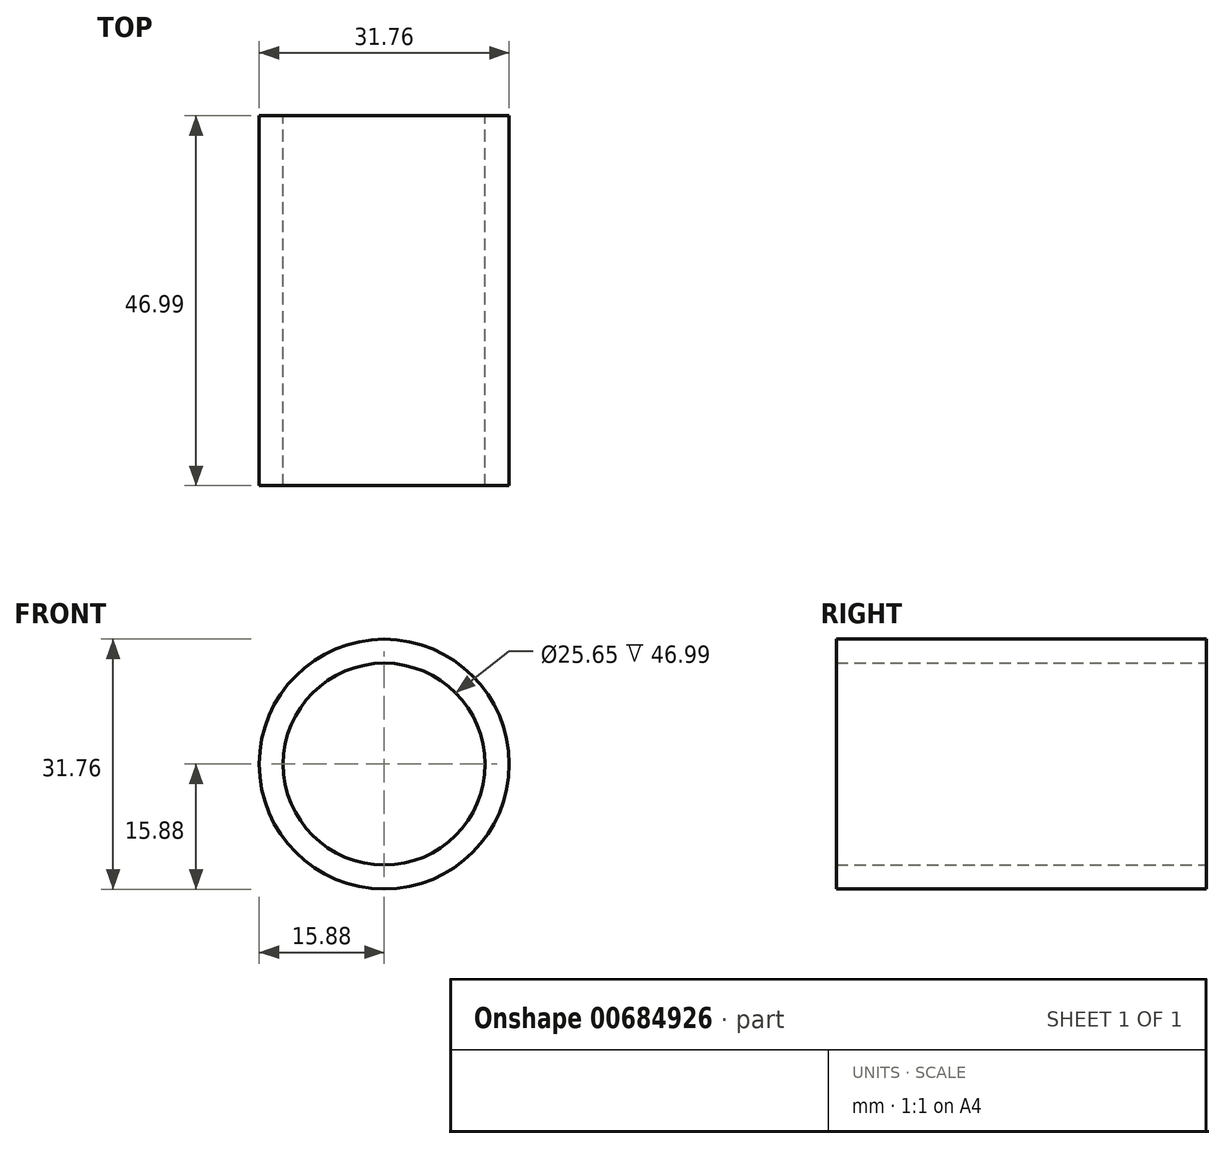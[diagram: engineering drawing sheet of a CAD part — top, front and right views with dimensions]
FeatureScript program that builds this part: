
annotation { "Feature Type Name" : "Feature", "Feature Type Description" : "" }
export const myFeature = defineFeature(function(context is Context, id is Id, definition is map)
    precondition{}
    {
        {
            var Q0;
            Q0=qCreatedBy(makeId("Front.planeOp"),FACE);
            var sketch = newSketch(context, id + "F0", { "sketchPlane" : qUnion([Q0])});
            skCircle(sketch, "E0", {"center": v(0, 0) * mm, "radius": 15.88 * mm});
            skCircle(sketch, "E1", {"center": v(0, 0) * mm, "radius": 12.83 * mm});
            skSolve(sketch);
        }
        {
            var Q0;
            Q0 = qSketchRegion(id + "F0", true);
            extrude(context, id + "F1", {"entities" : qUnion([Q0]), "depth" : 47 * mm, "offsetDistance" : 25.4 * mm});
        }
    });
